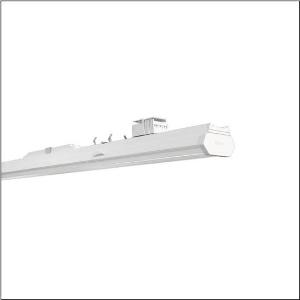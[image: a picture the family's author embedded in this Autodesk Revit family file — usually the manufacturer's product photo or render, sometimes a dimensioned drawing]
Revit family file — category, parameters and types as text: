
# Revit family: licross_11_protected_mo_51tp12cn685g
name_source: partatom
category: Lighting Fixtures
units: mm (PartAtom-declared; Revit-internal decimal feet)

## family parameters
Cut with Voids When Loaded = No
Host = Face
Light Source = No
Part Type = Normal
Room Calculation Point = No
Round Connector Dimension = Use Diameter
Shared = No

## types (1)
- --- (1 x LED, 8840 lm, 49.4 W, 6500K)
    Apparent Load = 49 VA
    CIE Flux Codes = 73 92 98 99 100
    Color Rendering = 80
    Color Temperature = 6500K
    Default Elevation = 1800 mm
    Description = Licross 11 Protected MO, luminaire insert, of sheet steel, galvanised, coil coated, white, length: 1.500mm, width: 90mm, height: 101mm, LED rated luminous flux: 8.840lm, light colour: 865, SDCM (Standard Deviation of Colour Matching)MacAdam ≤ 2 SDCM (initial), control gear: ON/OFF Multilumen, CLOi, with plug, 3-pole, with phase selection, mains connection: 220..240V, AC, 50/60Hz, start of lifetime: 49W, end of service life: 55W, internal wiring halogen-free, primary light control with lens, of plastic, primary optical cover: cover, of PMMA, light emission: direct distribution, primary light characteristic: symmetric, protection rating (complete): IP64, insulation class (complete): insulation class I (protective earthing), certification: CE, ENEC, VDE, UKCA, protection symbol: D if used in an environment with conductive dust loads with corresponding accessories, impact resistance: IK06, permissible ambient temperature for indoor applications: -35..+40°C, corresponds to IFS (International Featured Standards) requirements for safety and quality in the food industry, reducing of maximum allowable ambient temperature of 5°C with ceiling mounting, LABS conformity tested according to VDMA 24364:2018-05, The light source and the operating device comply with the requirements of the Ecodesign Regulation (EU) 2019/2020 and are replaceable in accordance with this regulation, packaging unit: 1 piece
    Height = 92 mm
    Lamp = 1 x LED
    Lamp Light Flux = 8840 lm
    Lamp Power = 49.4 W
    Lamp count = 1
    Length = 1500 mm
    Luminous efficacy = 179 lm/W
    Manufacturer = Siteco
    ModVariant = No
    Model = 51TP12CN685G
    Mounting Place = Ceiling
    Mounting Type = Pendant
    Number of Poles = 1
    OnlyDefault = Yes
    Power Factor = 1
    Product Name = Licross 11 Protected MO
    Product group = luminaire insert | ceiling pendant
    ProductGroupID = 901
    Protection Class = Protection class I
    Protection Degree = IP 64
    RLX_Detail_Level = 1
    RLX_Emergency_Light_Flux = 0 lm
    RLX_Emergency_Type = 0
    RLX_Emergency_Type_DB = No
    RlxData = <blob elided: 22369 chars, md5=85731c10>
    Socket = socket
    Standby Power = 0 W
    System Light Flux = 8840 lm
    System Power = 49 W
    Type Comments = factory setting: luminous flux: 100 % | (A | C | E) | 113 mA
    Type Image = l_1256148.jpg
    URL = http://relux.com
    VarID = @adj_000815
    Voltage = 0 V
    Weight = 0.00 kg
    Width = 88 mm

## geometry (parser evidence)
native form markers: Blend x4, Sweep x13
no freeform markers — native parametric forms only
